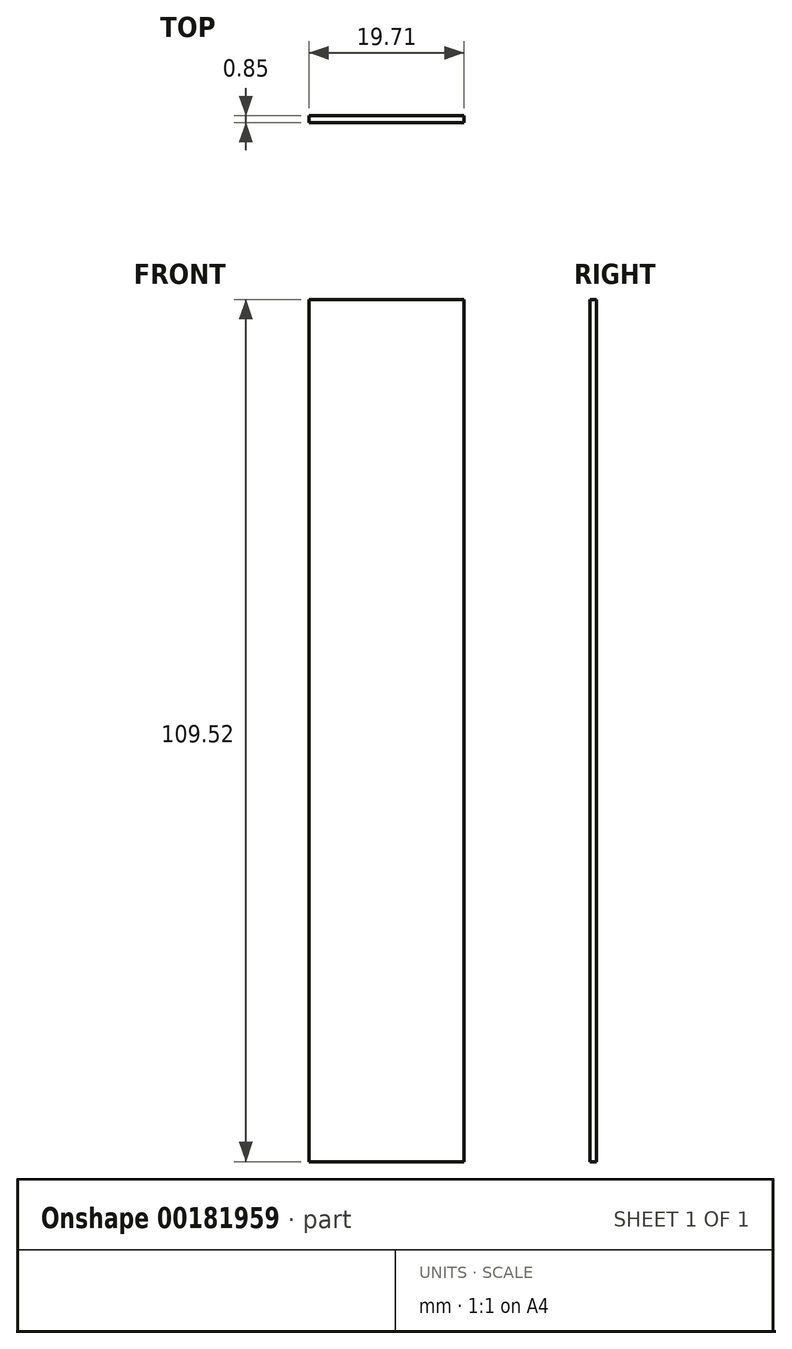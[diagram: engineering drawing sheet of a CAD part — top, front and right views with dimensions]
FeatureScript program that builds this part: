
annotation { "Feature Type Name" : "Feature", "Feature Type Description" : "" }
export const myFeature = defineFeature(function(context is Context, id is Id, definition is map)
    precondition{}
    {
        {
            var Q0;
            Q0=qCreatedBy(makeId("Front.planeOp"),FACE);
            var sketch = newSketch(context, id + "F0", { "sketchPlane" : qUnion([Q0])});
            skLineSegment(sketch, "E0.bottom", {"start": v(75.66, -75.36) * mm, "end": v(55.95, -75.36) * mm});
            skLineSegment(sketch, "E0.top", {"start": v(75.66, 34.16) * mm, "end": v(55.95, 34.16) * mm});
            skLineSegment(sketch, "E0.left", {"start": v(75.66, -75.36) * mm, "end": v(75.66, 34.16) * mm});
            skLineSegment(sketch, "E0.right", {"start": v(55.95, -75.36) * mm, "end": v(55.95, 34.16) * mm});
            skSolve(sketch);
        }
        {
            var Q0;
            Q0=makeQuery(id+"F0.imprint","IMPRINT",FACE,{"disambiguationData":[TD([[makeQuery(id+"F0.imprint","IMPRINT",EDGE,{"derivedFrom":sQuery(id+"F0.wireOp",EDGE,"E0.bottom")}),-1.0]])]});
            extrude(context, id + "F1", {"entities" : qUnion([Q0]), "depth" : 0.85 * mm});
        }
    });
